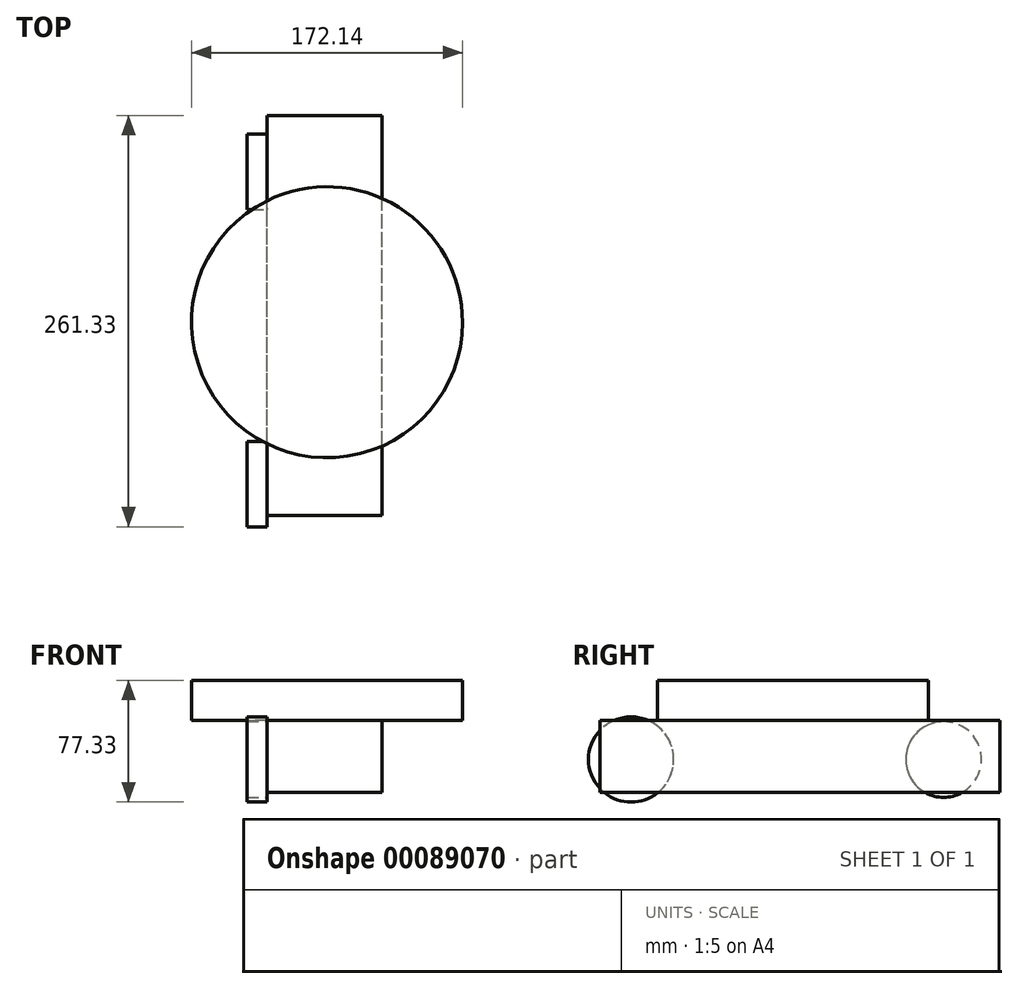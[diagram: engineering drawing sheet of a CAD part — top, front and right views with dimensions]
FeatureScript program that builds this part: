
annotation { "Feature Type Name" : "Feature", "Feature Type Description" : "" }
export const myFeature = defineFeature(function(context is Context, id is Id, definition is map)
    precondition{}
    {
        {
            var Q0;
            Q0=qCreatedBy(makeId("Front.planeOp"),FACE);
            var sketch = newSketch(context, id + "F0", { "sketchPlane" : qUnion([Q0])});
            skLineSegment(sketch, "E0", {"start": v(-38.22, 37.5) * mm, "end": v(35.08, 37.5) * mm});
            skLineSegment(sketch, "E1", {"start": v(35.08, 37.5) * mm, "end": v(35.08, -8.41) * mm});
            skLineSegment(sketch, "E2", {"start": v(35.08, -8.41) * mm, "end": v(-38.22, -8.41) * mm});
            skLineSegment(sketch, "E3", {"start": v(-38.22, -8.41) * mm, "end": v(-38.22, 37.5) * mm});
            skSolve(sketch);
        }
        {
            var Q0;
            Q0 = qSketchRegion(id + "F0", true);
            extrude(context, id + "F1", {"entities" : qUnion([Q0]), "depth" : 254 * mm});
        }
        {
            var Q0;
            Q0=makeQuery(id+"F1.opExtrude","SWEPT_FACE",FACE,{"disambiguationData":[OSD([sQuery(id+"F0.wireOp",EDGE,"E0")])]});
            var sketch = newSketch(context, id + "F2", { "sketchPlane" : qUnion([Q0])});
            skCircle(sketch, "E4", {"center": v(0, -131.4) * mm, "radius": 86.07 * mm});
            skSolve(sketch);
        }
        {
            var Q0;
            Q0 = qSketchRegion(id + "F2", true);
            extrude(context, id + "F3", {"entities" : qUnion([Q0]), "operationType" : NewBodyOperationType.ADD, "depth" : 25.4 * mm});
        }
        {
            var Q0;
            Q0=makeQuery(id+"F1.opExtrude","SWEPT_FACE",FACE,{"disambiguationData":[OSD([sQuery(id+"F0.wireOp",EDGE,"E3")])]});
            var sketch = newSketch(context, id + "F4", { "sketchPlane" : qUnion([Q0])});
            skCircle(sketch, "E5", {"center": v(234.27, 12.64) * mm, "radius": 27.06 * mm});
            skCircle(sketch, "E6", {"center": v(35.78, 12.64) * mm, "radius": 24.04 * mm});
            skSolve(sketch);
        }
        {
            var Q0;
            Q0 = qSketchRegion(id + "F4", true);
            extrude(context, id + "F5", {"entities" : qUnion([Q0]), "operationType" : NewBodyOperationType.ADD, "depth" : 12.7 * mm});
        }
    });
